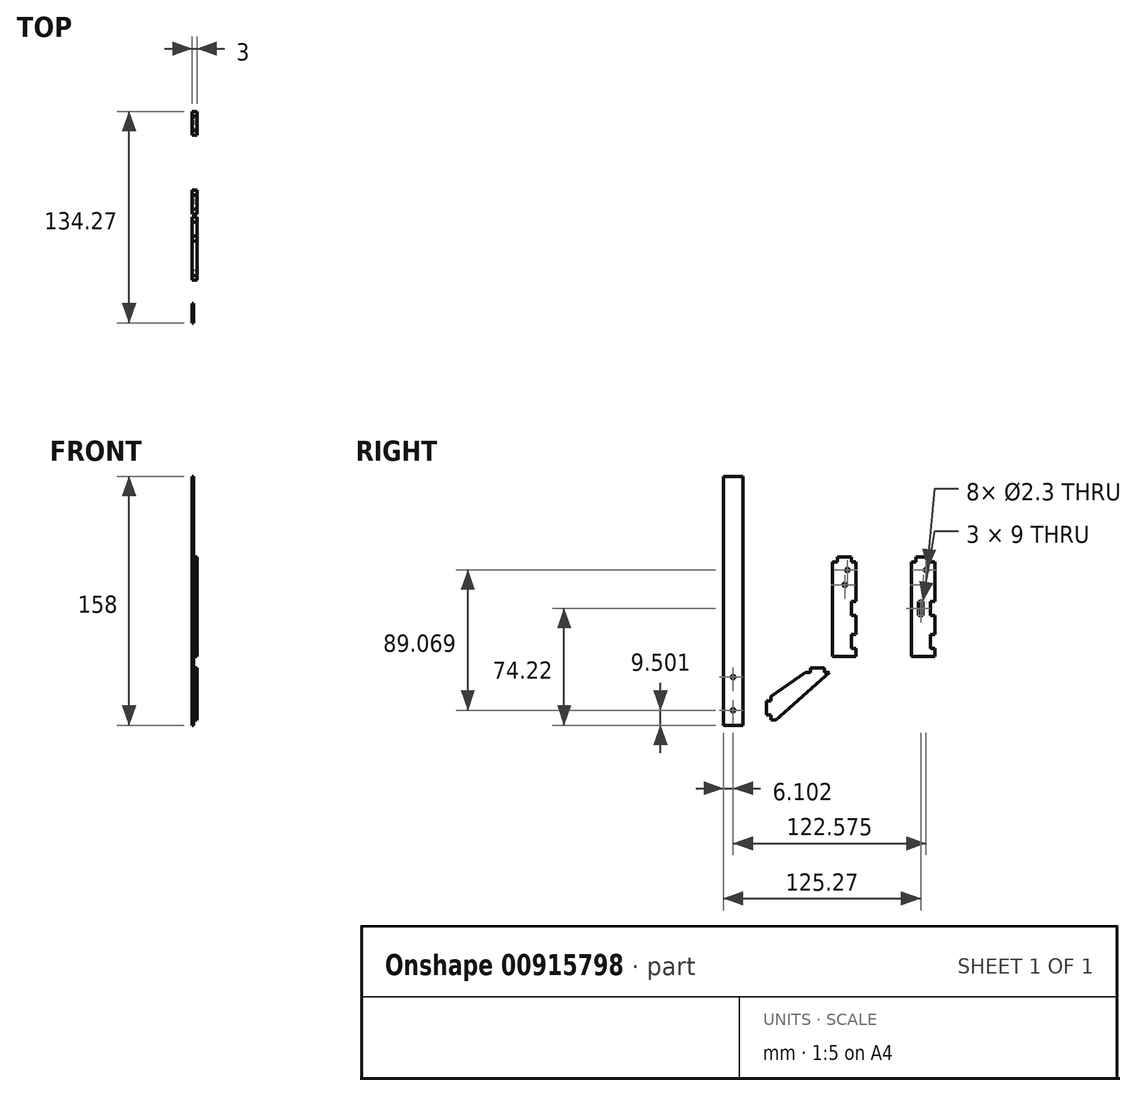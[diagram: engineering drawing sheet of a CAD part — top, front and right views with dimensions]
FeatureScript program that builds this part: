
annotation { "Feature Type Name" : "Feature", "Feature Type Description" : "" }
export const myFeature = defineFeature(function(context is Context, id is Id, definition is map)
    precondition{}
    {
        {
            var Q0;
            Q0=qCreatedBy(makeId("Right.planeOp"),FACE);
            var sketch = newSketch(context, id + "F0", { "sketchPlane" : qUnion([Q0])});
            skLineSegment(sketch, "E0.bottom", {"start": v(0, 60) * mm, "end": v(15, 60) * mm});
            skLineSegment(sketch, "E0.top", {"start": v(0, 0) * mm, "end": v(15, 0) * mm});
            skLineSegment(sketch, "E0.left", {"start": v(0, 60) * mm, "end": v(0, 0) * mm});
            skLineSegment(sketch, "E0.right", {"start": v(15, 60) * mm, "end": v(15, 0) * mm});
            skCircle(sketch, "E1", {"center": v(9.4, 54.85) * mm, "radius": 1.15 * mm});
            skCircle(sketch, "E2", {"center": v(7.75, 45.45) * mm, "radius": 1.15 * mm});
            skSolve(sketch);
        }
        {
            var Q0;
            Q0 = qSketchRegion(id + "F0", true);
            extrude(context, id + "F1", {"entities" : qUnion([Q0]), "depth" : 3 * mm, "offsetDistance" : 25 * mm});
        }
        {
            var Q0;
            Q0=makeQuery(id+"F1.opExtrude","CAP_FACE",FACE,{"disambiguationData":[OSD([sQuery(id+"F0.wireOp",EDGE,"E0.bottom"),sQuery(id+"F0.wireOp",EDGE,"E0.top"),sQuery(id+"F0.wireOp",EDGE,"E0.left"),sQuery(id+"F0.wireOp",EDGE,"E0.right"),sQuery(id+"F0.wireOp",EDGE,"E1"),sQuery(id+"F0.wireOp",EDGE,"E2")])],"isStart":false});
            var sketch = newSketch(context, id + "F2", { "sketchPlane" : qUnion([Q0])});
            skLineSegment(sketch, "E3.bottom", {"start": v(15, 35) * mm, "end": v(12, 35) * mm});
            skLineSegment(sketch, "E3.top", {"start": v(15, 26) * mm, "end": v(12, 26) * mm});
            skLineSegment(sketch, "E3.left", {"start": v(15, 35) * mm, "end": v(15, 26) * mm});
            skLineSegment(sketch, "E3.right", {"start": v(12, 35) * mm, "end": v(12, 26) * mm});
            skLineSegment(sketch, "E4.bottom", {"start": v(12, 14) * mm, "end": v(15, 14) * mm});
            skLineSegment(sketch, "E4.top", {"start": v(12, 5) * mm, "end": v(15, 5) * mm});
            skLineSegment(sketch, "E4.left", {"start": v(12, 14) * mm, "end": v(12, 5) * mm});
            skLineSegment(sketch, "E4.right", {"start": v(15, 14) * mm, "end": v(15, 5) * mm});
            skSolve(sketch);
        }
        {
            var Q0;
            Q0 = qSketchRegion(id + "F2", true);
            extrude(context, id + "F3", {"entities" : qUnion([Q0]), "operationType" : NewBodyOperationType.REMOVE, "oppositeDirection" : true, "depth" : 25 * mm, "offsetDistance" : 25 * mm});
        }
        {
            var Q0;
            Q0=makeQuery(id+"F1.opExtrude","CAP_FACE",FACE,{"disambiguationData":[OSD([sQuery(id+"F0.wireOp",EDGE,"E0.bottom"),sQuery(id+"F0.wireOp",EDGE,"E0.top"),sQuery(id+"F0.wireOp",EDGE,"E0.left"),sQuery(id+"F0.wireOp",EDGE,"E0.right"),sQuery(id+"F0.wireOp",EDGE,"E1"),sQuery(id+"F0.wireOp",EDGE,"E2")])],"isStart":false});
            var sketch = newSketch(context, id + "F4", { "sketchPlane" : qUnion([Q0])});
            skLineSegment(sketch, "E5.bottom", {"start": v(3, 60) * mm, "end": v(12, 60) * mm});
            skLineSegment(sketch, "E5.top", {"start": v(3, 63) * mm, "end": v(12, 63) * mm});
            skLineSegment(sketch, "E5.left", {"start": v(3, 60) * mm, "end": v(3, 63) * mm});
            skLineSegment(sketch, "E5.right", {"start": v(12, 60) * mm, "end": v(12, 63) * mm});
            skPoint(sketch, "E6", {"position": v(7.5, 60) * mm});
            skSolve(sketch);
        }
        {
            var Q0;
            Q0 = qSketchRegion(id + "F4", true);
            extrude(context, id + "F5", {"entities" : qUnion([Q0]), "operationType" : NewBodyOperationType.ADD, "oppositeDirection" : true, "depth" : 3 * mm, "offsetDistance" : 25 * mm});
        }
        {
            var Q0;
            Q0=makeQuery(id+"F1.opExtrude","SWEPT_BODY",BODY,{"disambiguationData":[OSD([sQuery(id+"F0.wireOp",EDGE,"E0.bottom"),sQuery(id+"F0.wireOp",EDGE,"E0.top"),sQuery(id+"F0.wireOp",EDGE,"E0.left"),sQuery(id+"F0.wireOp",EDGE,"E0.right"),sQuery(id+"F0.wireOp",EDGE,"E1"),sQuery(id+"F0.wireOp",EDGE,"E2")])]});
            transform(context, id + "F6", {"entities" : qUnion([Q0]), "transformType" : TransformType.TRANSLATION_3D, "dx" : 0 * mm, "dy" : 50 * mm, "dz" : 0 * mm, "makeCopy" : true});
        }
        {
            var Q0;
            Q0=makeQuery(id+"F6.opPattern","COPY",FACE,{"derivedFrom":makeQuery(id+"F5.boolean.opBoolean","MERGE",FACE,{"derivedFrom":[makeQuery(id+"F1.opExtrude","CAP_FACE",FACE,{"disambiguationData":[OSD([sQuery(id+"F0.wireOp",EDGE,"E0.bottom"),sQuery(id+"F0.wireOp",EDGE,"E0.top"),sQuery(id+"F0.wireOp",EDGE,"E0.left"),sQuery(id+"F0.wireOp",EDGE,"E0.right"),sQuery(id+"F0.wireOp",EDGE,"E1"),sQuery(id+"F0.wireOp",EDGE,"E2")])],"isStart":false}),makeQuery(id+"F5.opExtrude","CAP_FACE",FACE,{"disambiguationData":[OSD([sQuery(id+"F4.wireOp",EDGE,"E5.bottom"),sQuery(id+"F4.wireOp",EDGE,"E5.top"),sQuery(id+"F4.wireOp",EDGE,"E5.left"),sQuery(id+"F4.wireOp",EDGE,"E5.right")])],"isStart":true})]}),"instanceName":"1"});
            var sketch = newSketch(context, id + "F7", { "sketchPlane" : qUnion([Q0])});
            skLineSegment(sketch, "E7.bottom", {"start": v(54.5, 35) * mm, "end": v(57.5, 35) * mm});
            skLineSegment(sketch, "E7.top", {"start": v(54.5, 26) * mm, "end": v(57.5, 26) * mm});
            skLineSegment(sketch, "E7.left", {"start": v(54.5, 35) * mm, "end": v(54.5, 26) * mm});
            skLineSegment(sketch, "E7.right", {"start": v(57.5, 35) * mm, "end": v(57.5, 26) * mm});
            skLineSegment(sketch, "E8", {"start": v(50, 32.79) * mm, "end": v(62, 32.79) * mm, "construction": true});
            skPoint(sketch, "E9", {"position": v(56, 32.79) * mm});
            skPoint(sketch, "E10", {"position": v(56, 26) * mm});
            skSolve(sketch);
        }
        {
            var Q0;
            Q0 = qSketchRegion(id + "F7", true);
            extrude(context, id + "F8", {"entities" : qUnion([Q0]), "operationType" : NewBodyOperationType.REMOVE, "oppositeDirection" : true, "depth" : 25 * mm, "offsetDistance" : 25 * mm});
        }
        {
            var Q0;
            Q0=makeQuery(id+"F1.opExtrude","SWEPT_BODY",BODY,{"disambiguationData":[OSD([sQuery(id+"F0.wireOp",EDGE,"E0.bottom"),sQuery(id+"F0.wireOp",EDGE,"E0.top"),sQuery(id+"F0.wireOp",EDGE,"E0.left"),sQuery(id+"F0.wireOp",EDGE,"E0.right"),sQuery(id+"F0.wireOp",EDGE,"E1"),sQuery(id+"F0.wireOp",EDGE,"E2")])]});
            transform(context, id + "F9", {"entities" : qUnion([Q0]), "transformType" : TransformType.TRANSLATION_3D, "dx" : 0 * mm, "dy" : 0 * mm, "dz" : 0 * mm, "makeCopy" : true});
        }
        {
            var Q0;
            Q0=qCreatedBy(makeId("Right.planeOp"),FACE);
            var sketch = newSketch(context, id + "F10", { "sketchPlane" : qUnion([Q0])});
            skLineSegment(sketch, "E11", {"start": v(-17.1, -10.3) * mm, "end": v(-14.1, -10.3) * mm});
            skLineSegment(sketch, "E12", {"start": v(-2.1, -10.3) * mm, "end": v(-36.1, -40.3) * mm});
            skLineSegment(sketch, "E13", {"start": v(-39.1, -40.3) * mm, "end": v(-39.1, -37.3) * mm});
            skLineSegment(sketch, "E14.top", {"start": v(-14.1, -7.3) * mm, "end": v(-5.1, -7.3) * mm});
            skLineSegment(sketch, "E14.left", {"start": v(-14.1, -10.3) * mm, "end": v(-14.1, -7.3) * mm});
            skLineSegment(sketch, "E14.right", {"start": v(-5.1, -10.3) * mm, "end": v(-5.1, -7.3) * mm});
            skLineSegment(sketch, "E15.trimOffspring", {"start": v(-5.1, -10.3) * mm, "end": v(-2.1, -10.3) * mm});
            skLineSegment(sketch, "E16.bottom", {"start": v(-39.1, -37.3) * mm, "end": v(-42.1, -37.3) * mm});
            skLineSegment(sketch, "E16.top", {"start": v(-39.1, -28.3) * mm, "end": v(-42.1, -28.3) * mm});
            skLineSegment(sketch, "E16.right", {"start": v(-42.1, -37.3) * mm, "end": v(-42.1, -28.3) * mm});
            skLineSegment(sketch, "E17", {"start": v(-39.1, -40.3) * mm, "end": v(-36.1, -40.3) * mm});
            skPoint(sketch, "E18.orphan", {"position": v(-39.1, -42.95) * mm});
            skLineSegment(sketch, "E19", {"start": v(-39.1, -25.3) * mm, "end": v(-17.1, -10.3) * mm});
            skPoint(sketch, "E20.orphan", {"position": v(-39.1, -10.3) * mm});
            skLineSegment(sketch, "E21.trimOffspring", {"start": v(-39.1, -28.3) * mm, "end": v(-39.1, -25.3) * mm});
            skSolve(sketch);
        }
        {
            var Q0;
            Q0 = qSketchRegion(id + "F10", true);
            extrude(context, id + "F11", {"entities" : qUnion([Q0]), "depth" : 3 * mm, "offsetDistance" : 25 * mm});
        }
        {
            var Q0;
            Q0=qCreatedBy(makeId("Right.planeOp"),FACE);
            var sketch = newSketch(context, id + "F12", { "sketchPlane" : qUnion([Q0])});
            skLineSegment(sketch, "E22.bottom", {"start": v(-69.27, 114.28) * mm, "end": v(-57.07, 114.28) * mm});
            skLineSegment(sketch, "E22.top", {"start": v(-69.27, -43.72) * mm, "end": v(-57.07, -43.72) * mm});
            skLineSegment(sketch, "E22.left", {"start": v(-69.27, 114.28) * mm, "end": v(-69.27, -43.72) * mm});
            skLineSegment(sketch, "E22.right", {"start": v(-57.07, 114.28) * mm, "end": v(-57.07, -43.72) * mm});
            skCircle(sketch, "E23", {"center": v(-63.17, -34.22) * mm, "radius": 1.15 * mm});
            skCircle(sketch, "E24", {"center": v(-63.17, -13.22) * mm, "radius": 1.15 * mm});
            skPoint(sketch, "E25", {"position": v(-63.17, -43.72) * mm});
            skSolve(sketch);
        }
        {
            var Q0;
            Q0 = qSketchRegion(id + "F12", true);
            extrude(context, id + "F13", {"entities" : qUnion([Q0]), "depth" : 0.8 * mm, "offsetDistance" : 25 * mm});
        }
    });
